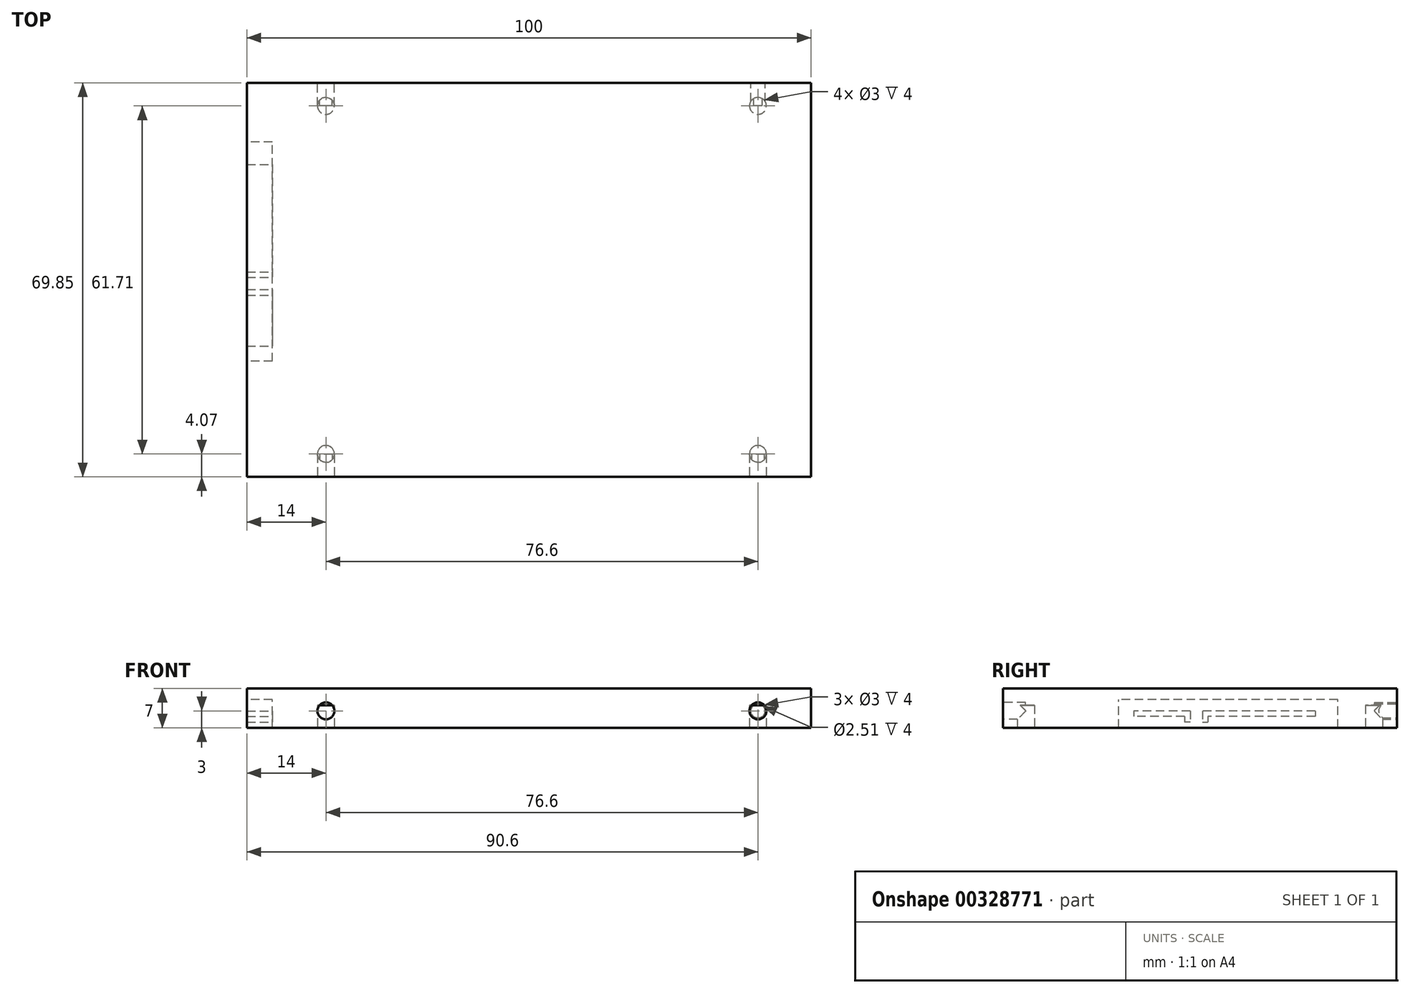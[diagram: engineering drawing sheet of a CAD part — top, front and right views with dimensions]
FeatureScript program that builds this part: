
annotation { "Feature Type Name" : "Feature", "Feature Type Description" : "" }
export const myFeature = defineFeature(function(context is Context, id is Id, definition is map)
    precondition{}
    {
        {
            var Q0;
            Q0=qCreatedBy(makeId("Top.planeOp"),FACE);
            var sketch = newSketch(context, id + "F0", { "sketchPlane" : qUnion([Q0])});
            skLineSegment(sketch, "E0.bottom", {"start": v(0, 0) * mm, "end": v(100, 0) * mm});
            skLineSegment(sketch, "E0.top", {"start": v(0, 69.85) * mm, "end": v(100, 69.85) * mm});
            skLineSegment(sketch, "E0.left", {"start": v(0, 0) * mm, "end": v(0, 69.85) * mm});
            skLineSegment(sketch, "E0.right", {"start": v(100, 0) * mm, "end": v(100, 69.85) * mm});
            skSolve(sketch);
        }
        {
            var Q0;
            Q0 = qSketchRegion(id + "F0", true);
            extrude(context, id + "F1", {"entities" : qUnion([Q0]), "depth" : 7 * mm});
        }
        {
            var Q0;
            Q0=makeQuery(id+"F1.opExtrude","SWEPT_FACE",FACE,{"disambiguationData":[OSD([sQuery(id+"F0.wireOp",EDGE,"E0.left")])]});
            var sketch = newSketch(context, id + "F2", { "sketchPlane" : qUnion([Q0])});
            skLineSegment(sketch, "E1.bottom", {"start": v(-59.35, 0) * mm, "end": v(-20.5, 0) * mm});
            skLineSegment(sketch, "E1.top", {"start": v(-59.35, 5) * mm, "end": v(-20.5, 5) * mm});
            skLineSegment(sketch, "E1.left", {"start": v(-59.35, 0) * mm, "end": v(-59.35, 5) * mm});
            skLineSegment(sketch, "E1.right", {"start": v(-20.5, 0) * mm, "end": v(-20.5, 5) * mm});
            skSolve(sketch);
        }
        {
            var Q0;
            Q0=makeQuery(id+"F2.imprint","IMPRINT",FACE,{"disambiguationData":[TD([[makeQuery(id+"F2.imprint","IMPRINT",EDGE,{"derivedFrom":sQuery(id+"F2.wireOp",EDGE,"E1.bottom")}),-1.0]])]});
            extrude(context, id + "F3", {"entities" : qUnion([Q0]), "operationType" : NewBodyOperationType.REMOVE, "oppositeDirection" : true, "depth" : 4.5 * mm});
        }
        {
            var Q0;
            Q0=makeQuery(id+"F3.boolean.opBoolean","COPY",FACE,{"derivedFrom":makeQuery(id+"F3.opExtrude","CAP_FACE",FACE,{"disambiguationData":[OSD([sQuery(id+"F2.wireOp",EDGE,"E1.bottom"),sQuery(id+"F2.wireOp",EDGE,"E1.top"),sQuery(id+"F2.wireOp",EDGE,"E1.left"),sQuery(id+"F2.wireOp",EDGE,"E1.right")])],"isStart":false})});
            var sketch = newSketch(context, id + "F4", { "sketchPlane" : qUnion([Q0])});
            skLineSegment(sketch, "E2.bottom", {"start": v(-55.35, 3) * mm, "end": v(-35.35, 3) * mm});
            skLineSegment(sketch, "E2.top", {"start": v(-55.35, 2) * mm, "end": v(-36.35, 2) * mm});
            skLineSegment(sketch, "E2.left", {"start": v(-55.35, 3) * mm, "end": v(-55.35, 2) * mm});
            skLineSegment(sketch, "E2.right", {"start": v(-35.35, 3) * mm, "end": v(-35.35, 2) * mm});
            skLineSegment(sketch, "E3.top", {"start": v(-35.35, 1) * mm, "end": v(-36.35, 1) * mm});
            skLineSegment(sketch, "E3.left", {"start": v(-35.35, 2) * mm, "end": v(-35.35, 1) * mm});
            skLineSegment(sketch, "E3.right", {"start": v(-36.35, 2) * mm, "end": v(-36.35, 1) * mm});
            skLineSegment(sketch, "E4.bottom", {"start": v(-33.2, 3) * mm, "end": v(-23.2, 3) * mm});
            skLineSegment(sketch, "E4.top", {"start": v(-33.2, 2) * mm, "end": v(-23.2, 2) * mm});
            skLineSegment(sketch, "E4.left", {"start": v(-33.2, 3) * mm, "end": v(-33.2, 2) * mm});
            skLineSegment(sketch, "E4.right", {"start": v(-23.2, 3) * mm, "end": v(-23.2, 2) * mm});
            skLineSegment(sketch, "E5.bottom", {"start": v(-33.2, 2) * mm, "end": v(-32.2, 2) * mm});
            skLineSegment(sketch, "E5.top", {"start": v(-33.2, 1) * mm, "end": v(-32.2, 1) * mm});
            skLineSegment(sketch, "E5.left", {"start": v(-33.2, 2) * mm, "end": v(-33.2, 1) * mm});
            skLineSegment(sketch, "E5.right", {"start": v(-32.2, 2) * mm, "end": v(-32.2, 1) * mm});
            skLineSegment(sketch, "E6", {"start": v(-35.35, 3) * mm, "end": v(-33.2, 3) * mm, "construction": true});
            skLineSegment(sketch, "E7", {"start": v(-35.35, 2) * mm, "end": v(-33.2, 2) * mm, "construction": true});
            skLineSegment(sketch, "E8", {"start": v(-35.35, 1) * mm, "end": v(-33.2, 1) * mm, "construction": true});
            skSolve(sketch);
        }
        {
            var Q0;
            Q0 = qSketchRegion(id + "F4", true);
            extrude(context, id + "F5", {"entities" : qUnion([Q0]), "operationType" : NewBodyOperationType.ADD, "depth" : 4.5 * mm});
        }
        {
            var Q0;
            Q0=makeQuery(id+"F1.opExtrude","CAP_FACE",FACE,{"disambiguationData":[OSD([sQuery(id+"F0.wireOp",EDGE,"E0.bottom"),sQuery(id+"F0.wireOp",EDGE,"E0.top"),sQuery(id+"F0.wireOp",EDGE,"E0.left"),sQuery(id+"F0.wireOp",EDGE,"E0.right")])],"isStart":true});
            var sketch = newSketch(context, id + "F6", { "sketchPlane" : qUnion([Q0])});
            skCircle(sketch, "E9", {"center": v(14, -65.78) * mm, "radius": 1.5 * mm});
            skCircle(sketch, "E10", {"center": v(14, -4.07) * mm, "radius": 1.5 * mm});
            skCircle(sketch, "E11", {"center": v(90.6, -65.78) * mm, "radius": 1.5 * mm});
            skCircle(sketch, "E12", {"center": v(90.6, -4.07) * mm, "radius": 1.5 * mm});
            skLineSegment(sketch, "E13", {"start": v(14, -65.78) * mm, "end": v(90.6, -65.78) * mm, "construction": true});
            skLineSegment(sketch, "E14", {"start": v(14, -65.78) * mm, "end": v(14, -4.07) * mm, "construction": true});
            skLineSegment(sketch, "E15", {"start": v(90.6, -4.07) * mm, "end": v(14, -4.07) * mm, "construction": true});
            skLineSegment(sketch, "E16", {"start": v(90.6, -4.07) * mm, "end": v(90.6, -65.78) * mm, "construction": true});
            skSolve(sketch);
        }
        {
            var Q0;
            Q0 = qSketchRegion(id + "F6", true);
            extrude(context, id + "F7", {"entities" : qUnion([Q0]), "operationType" : NewBodyOperationType.REMOVE, "oppositeDirection" : true, "depth" : 4 * mm});
        }
        {
            var Q0;
            Q0=makeQuery(id+"F1.opExtrude","SWEPT_FACE",FACE,{"disambiguationData":[OSD([sQuery(id+"F0.wireOp",EDGE,"E0.top")])]});
            var sketch = newSketch(context, id + "F8", { "sketchPlane" : qUnion([Q0])});
            skCircle(sketch, "E17", {"center": v(-14, 3) * mm, "radius": 1.5 * mm});
            skCircle(sketch, "E18", {"center": v(-90.6, 3) * mm, "radius": 1.26 * mm});
            skLineSegment(sketch, "E19", {"start": v(-14, 3) * mm, "end": v(-90.6, 3) * mm, "construction": true});
            skSolve(sketch);
        }
        {
            var Q0;
            Q0 = qSketchRegion(id + "F8", true);
            extrude(context, id + "F9", {"entities" : qUnion([Q0]), "operationType" : NewBodyOperationType.REMOVE, "oppositeDirection" : true, "depth" : 4 * mm});
        }
        {
            var Q0;
            Q0=makeQuery(id+"F1.opExtrude","SWEPT_FACE",FACE,{"disambiguationData":[OSD([sQuery(id+"F0.wireOp",EDGE,"E0.bottom")])]});
            var sketch = newSketch(context, id + "F10", { "sketchPlane" : qUnion([Q0])});
            skCircle(sketch, "E20", {"center": v(90.6, 3) * mm, "radius": 1.5 * mm});
            skCircle(sketch, "E21", {"center": v(14, 3) * mm, "radius": 1.5 * mm});
            skLineSegment(sketch, "E22", {"start": v(90.6, 3) * mm, "end": v(14, 3) * mm, "construction": true});
            skSolve(sketch);
        }
        {
            var Q0;
            Q0 = qSketchRegion(id + "F10", true);
            extrude(context, id + "F11", {"entities" : qUnion([Q0]), "operationType" : NewBodyOperationType.REMOVE, "oppositeDirection" : true, "depth" : 4 * mm});
        }
    });
